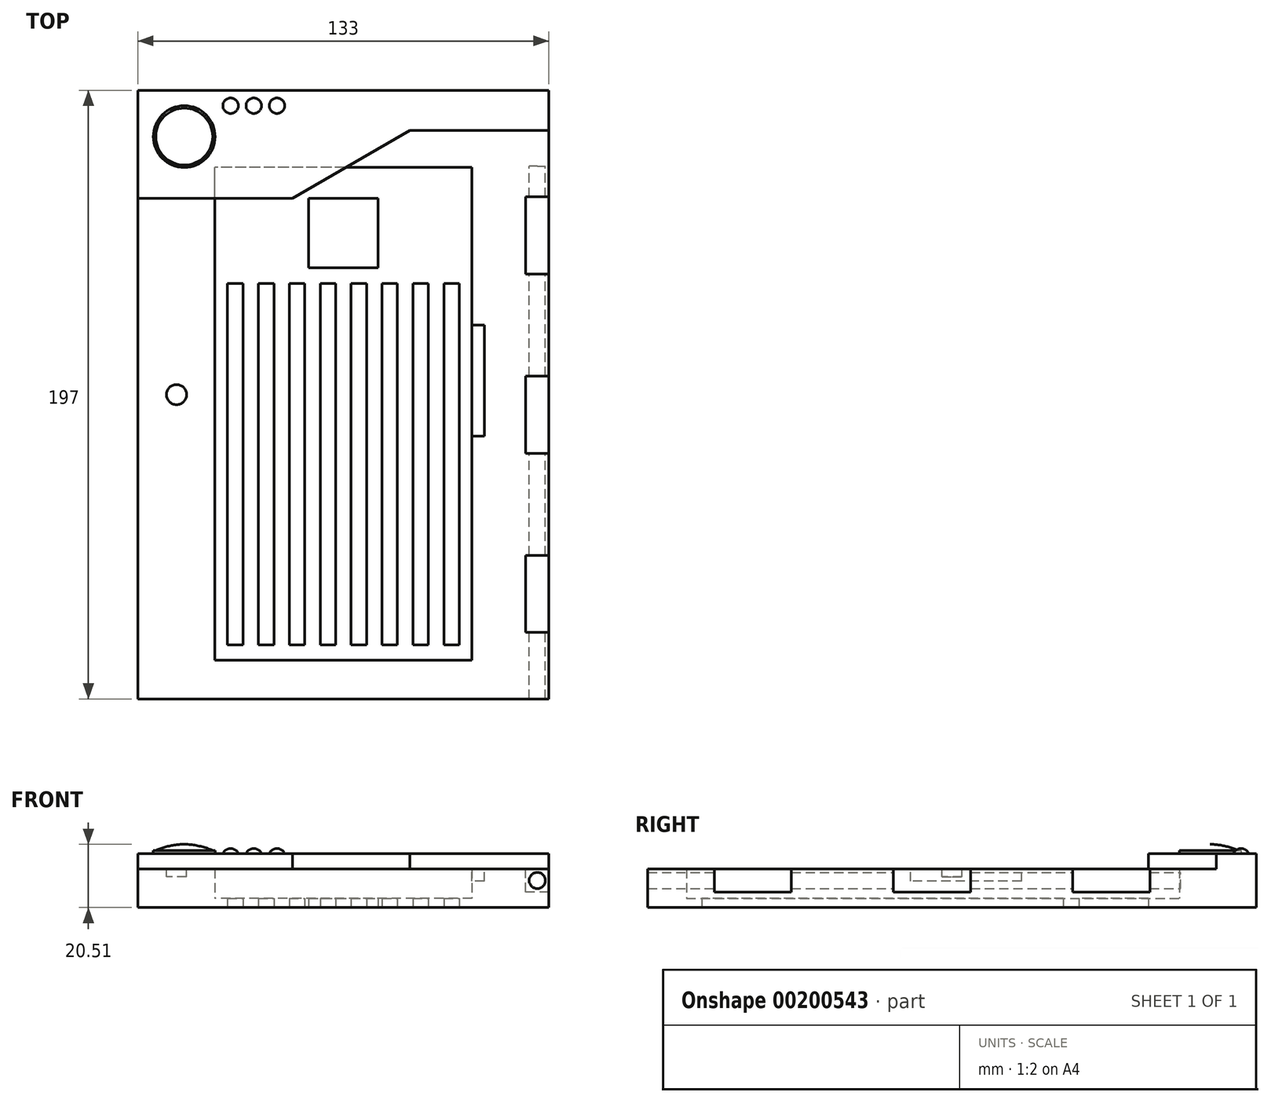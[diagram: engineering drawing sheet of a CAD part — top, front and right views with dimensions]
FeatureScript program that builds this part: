
annotation { "Feature Type Name" : "Feature", "Feature Type Description" : "" }
export const myFeature = defineFeature(function(context is Context, id is Id, definition is map)
    precondition{}
    {
        {
            var Q0;
            Q0=qCreatedBy(makeId("Top.planeOp"),FACE);
            var sketch = newSketch(context, id + "F0", { "sketchPlane" : qUnion([Q0])});
            skLineSegment(sketch, "E0.bottom", {"start": v(-77.75, 90.01) * mm, "end": v(55.25, 90.01) * mm});
            skLineSegment(sketch, "E0.top", {"start": v(-77.75, -106.99) * mm, "end": v(55.25, -106.99) * mm});
            skLineSegment(sketch, "E0.left", {"start": v(-77.75, 90.01) * mm, "end": v(-77.75, -106.99) * mm});
            skLineSegment(sketch, "E0.right", {"start": v(55.25, 90.01) * mm, "end": v(55.25, -106.99) * mm});
            skLineSegment(sketch, "E1.bottom", {"start": v(-52.88, 65.01) * mm, "end": v(30.38, 65.01) * mm});
            skLineSegment(sketch, "E1.top", {"start": v(-52.88, -94.49) * mm, "end": v(30.37, -94.49) * mm});
            skLineSegment(sketch, "E1.left", {"start": v(-52.88, 65.01) * mm, "end": v(-52.88, -94.49) * mm});
            skLineSegment(sketch, "E1.right", {"start": v(30.38, 65.01) * mm, "end": v(30.37, -94.49) * mm});
            skLineSegment(sketch, "E2", {"start": v(-77.75, 24.15) * mm, "end": v(-52.88, 24.15) * mm, "construction": true});
            skLineSegment(sketch, "E3", {"start": v(30.38, 23.5) * mm, "end": v(55.25, 23.5) * mm, "construction": true});
            skLineSegment(sketch, "E4.bottom", {"start": v(-22.5, 55.01) * mm, "end": v(0, 55.01) * mm});
            skLineSegment(sketch, "E4.top", {"start": v(-22.5, 32.51) * mm, "end": v(0, 32.51) * mm});
            skLineSegment(sketch, "E4.left", {"start": v(-22.5, 55.01) * mm, "end": v(-22.5, 32.51) * mm});
            skLineSegment(sketch, "E4.right", {"start": v(0, 55.01) * mm, "end": v(0, 32.51) * mm});
            skLineSegment(sketch, "E5", {"start": v(-22.5, 43.76) * mm, "end": v(-52.88, 43.76) * mm, "construction": true});
            skLineSegment(sketch, "E6", {"start": v(0, 43.76) * mm, "end": v(30.38, 43.76) * mm, "construction": true});
            skPoint(sketch, "E7.oppositeSnap0", {"position": v(30.37, -14.74) * mm});
            skLineSegment(sketch, "E8.bottom", {"start": v(-48.75, 27.51) * mm, "end": v(-43.75, 27.51) * mm});
            skLineSegment(sketch, "E8.top", {"start": v(-48.75, -89.49) * mm, "end": v(-43.75, -89.49) * mm});
            skLineSegment(sketch, "E8.left", {"start": v(-48.75, 27.51) * mm, "end": v(-48.75, -89.49) * mm});
            skLineSegment(sketch, "E8.right", {"start": v(-43.75, 27.51) * mm, "end": v(-43.75, -89.49) * mm});
            skLineSegment(sketch, "E9.1.0.0", {"start": v(-38.75, 27.51) * mm, "end": v(-38.75, -89.49) * mm});
            skLineSegment(sketch, "E9.1.0.1", {"start": v(-33.75, 27.51) * mm, "end": v(-33.75, -89.49) * mm});
            skLineSegment(sketch, "E9.1.0.2", {"start": v(-38.75, 27.51) * mm, "end": v(-33.75, 27.51) * mm});
            skLineSegment(sketch, "E9.1.0.3", {"start": v(-38.75, -89.49) * mm, "end": v(-33.75, -89.49) * mm});
            skLineSegment(sketch, "E9.2.0.0", {"start": v(-28.75, 27.51) * mm, "end": v(-28.75, -89.49) * mm});
            skLineSegment(sketch, "E9.2.0.1", {"start": v(-23.75, 27.51) * mm, "end": v(-23.75, -89.49) * mm});
            skLineSegment(sketch, "E9.2.0.2", {"start": v(-28.75, 27.51) * mm, "end": v(-23.75, 27.51) * mm});
            skLineSegment(sketch, "E9.2.0.3", {"start": v(-28.75, -89.49) * mm, "end": v(-23.75, -89.49) * mm});
            skLineSegment(sketch, "E9.3.0.0", {"start": v(-18.75, 27.51) * mm, "end": v(-18.75, -89.49) * mm});
            skLineSegment(sketch, "E9.3.0.1", {"start": v(-13.75, 27.51) * mm, "end": v(-13.75, -89.49) * mm});
            skLineSegment(sketch, "E9.3.0.2", {"start": v(-18.75, 27.51) * mm, "end": v(-13.75, 27.51) * mm});
            skLineSegment(sketch, "E9.3.0.3", {"start": v(-18.75, -89.49) * mm, "end": v(-13.75, -89.49) * mm});
            skLineSegment(sketch, "E9.4.0.0", {"start": v(-8.75, 27.51) * mm, "end": v(-8.75, -89.49) * mm});
            skLineSegment(sketch, "E9.4.0.1", {"start": v(-3.75, 27.51) * mm, "end": v(-3.75, -89.49) * mm});
            skLineSegment(sketch, "E9.4.0.2", {"start": v(-8.75, 27.51) * mm, "end": v(-3.75, 27.51) * mm});
            skLineSegment(sketch, "E9.4.0.3", {"start": v(-8.75, -89.49) * mm, "end": v(-3.75, -89.49) * mm});
            skLineSegment(sketch, "E9.5.0.0", {"start": v(1.25, 27.51) * mm, "end": v(1.25, -89.49) * mm});
            skLineSegment(sketch, "E9.5.0.1", {"start": v(6.25, 27.51) * mm, "end": v(6.25, -89.49) * mm});
            skLineSegment(sketch, "E9.5.0.2", {"start": v(1.25, 27.51) * mm, "end": v(6.25, 27.51) * mm});
            skLineSegment(sketch, "E9.5.0.3", {"start": v(1.25, -89.49) * mm, "end": v(6.25, -89.49) * mm});
            skLineSegment(sketch, "E9.6.0.0", {"start": v(11.25, 27.51) * mm, "end": v(11.25, -89.49) * mm});
            skLineSegment(sketch, "E9.6.0.1", {"start": v(16.25, 27.51) * mm, "end": v(16.25, -89.49) * mm});
            skLineSegment(sketch, "E9.6.0.2", {"start": v(11.25, 27.51) * mm, "end": v(16.25, 27.51) * mm});
            skLineSegment(sketch, "E9.6.0.3", {"start": v(11.25, -89.49) * mm, "end": v(16.25, -89.49) * mm});
            skLineSegment(sketch, "E9.7.0.0", {"start": v(21.25, 27.51) * mm, "end": v(21.25, -89.49) * mm});
            skLineSegment(sketch, "E9.7.0.1", {"start": v(26.25, 27.51) * mm, "end": v(26.25, -89.49) * mm});
            skLineSegment(sketch, "E9.7.0.2", {"start": v(21.25, 27.51) * mm, "end": v(26.25, 27.51) * mm});
            skLineSegment(sketch, "E9.7.0.3", {"start": v(21.25, -89.49) * mm, "end": v(26.25, -89.49) * mm});
            skLineSegment(sketch, "E9.direction1", {"start": v(-48.75, -89.49) * mm, "end": v(-38.75, -89.49) * mm, "construction": true});
            skSolve(sketch);
        }
        {
            var Q0;
            Q0=makeQuery(id+"F0.imprint","IMPRINT",FACE,{"disambiguationData":[TD([[makeQuery(id+"F0.imprint","IMPRINT",EDGE,{"derivedFrom":sQuery(id+"F0.wireOp",EDGE,"E0.bottom")}),-1.0]])]});
            var Q1;
            Q1=makeQuery(id+"F0.imprint","IMPRINT",FACE,{"disambiguationData":[TD([[makeQuery(id+"F0.imprint","IMPRINT",EDGE,{"derivedFrom":sQuery(id+"F0.wireOp",EDGE,"E1.bottom")}),-1.0]])]});
            extrude(context, id + "F1", {"entities" : qUnion([Q0, Q1]), "depth" : 3 * mm});
        }
        {
            var Q0;
            Q0 = qSketchRegion(id + "F0", true);
            extrude(context, id + "F2", {"entities" : qUnion([Q0]), "operationType" : NewBodyOperationType.ADD, "depth" : 12.5 * mm});
        }
        {
            var Q0;
            Q0=makeQuery(id+"F2.opExtrude","CAP_FACE",FACE,{"disambiguationData":[OSD([sQuery(id+"F0.wireOp",EDGE,"E0.bottom"),sQuery(id+"F0.wireOp",EDGE,"E0.top"),sQuery(id+"F0.wireOp",EDGE,"E0.left"),sQuery(id+"F0.wireOp",EDGE,"E0.right"),sQuery(id+"F0.wireOp",EDGE,"E1.bottom"),sQuery(id+"F0.wireOp",EDGE,"E1.top"),sQuery(id+"F0.wireOp",EDGE,"E1.left"),sQuery(id+"F0.wireOp",EDGE,"E1.right")])],"isStart":false});
            var sketch = newSketch(context, id + "F3", { "sketchPlane" : qUnion([Q0])});
            skLineSegment(sketch, "E10", {"start": v(-65.25, 90.01) * mm, "end": v(-65.25, -11.74) * mm, "construction": true});
            skCircle(sketch, "E11", {"center": v(-65.25, -8.49) * mm, "radius": 3.25 * mm});
            skLineSegment(sketch, "E12.trimOffspring", {"start": v(-65.25, -5.24) * mm, "end": v(-65.25, -106.99) * mm, "construction": true});
            skLineSegment(sketch, "E13", {"start": v(-77.75, 55.01) * mm, "end": v(-27.75, 55.01) * mm});
            skLineSegment(sketch, "E14", {"start": v(-27.75, 55.01) * mm, "end": v(10.25, 77.01) * mm});
            skLineSegment(sketch, "E15", {"start": v(10.25, 77.01) * mm, "end": v(55.25, 77.01) * mm});
            skLineSegment(sketch, "E16", {"start": v(-77.75, 55.01) * mm, "end": v(-77.75, 90.01) * mm});
            skLineSegment(sketch, "E17", {"start": v(-77.75, 90.01) * mm, "end": v(55.25, 90.01) * mm});
            skLineSegment(sketch, "E18", {"start": v(55.25, 90.01) * mm, "end": v(55.25, 77.01) * mm});
            skSolve(sketch);
        }
        {
            var Q0;
            Q0=makeQuery(id+"F3.imprint","IMPRINT",FACE,{"disambiguationData":[TD([[makeQuery(id+"F3.imprint","IMPRINT",EDGE,{"derivedFrom":sQuery(id+"F3.wireOp",EDGE,"E11")}),1.0]])]});
            var Q1;
            {var subQ4=sQuery(id+"F3.wireOp",EDGE,"E15");Q1=makeQuery(id+"F3.imprint","IMPRINT",FACE,{"disambiguationData":[TD([[makeQuery(id+"F3.imprint","IMPRINT",EDGE,{"derivedFrom":subQ4}),1.0]])]});}
            extrude(context, id + "F4", {"entities" : qUnion([Q0, Q1]), "operationType" : NewBodyOperationType.REMOVE, "oppositeDirection" : true, "depth" : 2.5 * mm});
        }
        {
            var Q0;
            {var subQ4=sQuery(id+"F3.wireOp",EDGE,"E15");Q0=makeQuery(id+"F3.imprint","IMPRINT",FACE,{"disambiguationData":[TD([[makeQuery(id+"F3.imprint","IMPRINT",EDGE,{"derivedFrom":subQ4}),1.0]])]});}
            var Q1;
            {var subQ0=sQuery(id+"F3.wireOp",EDGE,"E14");var subQ1=sQuery(id+"F3.wireOp",EDGE,"E13");var subQ2=makeQuery(id+"F3.imprint","INTERSECT",VERTEX,{"derivedFrom":[subQ1,subQ0]});Q1=makeQuery(id+"F3.imprint","IMPRINT",FACE,{"disambiguationData":[TD([[makeQuery(id+"F3.imprint","IMPRINT",EDGE,{"disambiguationData":[TD([[subQ2,1.0]])],"derivedFrom":subQ1}),1.0]])]});}
            var Q2;
            Q2=makeQuery(id+"F4.boolean.opBoolean","COPY",FACE,{"derivedFrom":makeQuery(id+"F4.opExtrude","CAP_FACE",FACE,{"disambiguationData":[OSD([sQuery(id+"F3.wireOp",EDGE,"E13"),sQuery(id+"F3.wireOp",EDGE,"E14"),sQuery(id+"F3.wireOp",EDGE,"E15"),sQuery(id+"F3.wireOp",EDGE,"E16"),sQuery(id+"F3.wireOp",EDGE,"E17"),sQuery(id+"F3.wireOp",EDGE,"E18")])],"isStart":false})});
            extrude(context, id + "F5", {"entities" : qUnion([Q0, Q1, Q2]), "operationType" : NewBodyOperationType.ADD, "depth" : 5 * mm});
        }
        {
            var Q0;
            {var subQ0=sQuery(id+"F3.wireOp",EDGE,"E18");var subQ1=sQuery(id+"F3.wireOp",EDGE,"E17");var subQ2=sQuery(id+"F3.wireOp",EDGE,"E16");var subQ3=sQuery(id+"F3.wireOp",EDGE,"E15");var subQ4=sQuery(id+"F3.wireOp",EDGE,"E14");var subQ6=sQuery(id+"F3.wireOp",EDGE,"E13");var subQ7=makeQuery(id+"F3.imprint","INTERSECT",VERTEX,{"derivedFrom":[subQ6,subQ4]});var subQ8=makeQuery(id+"F3.imprint","INTERSECT",VERTEX,{"derivedFrom":[makeQuery(id+"F2.opExtrude","CAP_EDGE",EDGE,{"disambiguationData":[OSD([sQuery(id+"F0.wireOp",EDGE,"E1.left")])],"isStart":false}),subQ6]});Q0=makeQuery(id+"F5.opExtrude","CAP_FACE",FACE,{"disambiguationData":[OSD([subQ6,subQ4,subQ3,subQ2,subQ1,subQ0]),TDD([makeQuery(id+"F3.imprint","IMPRINT",EDGE,{"disambiguationData":[TD([[subQ8,1.0]])],"derivedFrom":subQ6}),makeQuery(id+"F3.imprint","IMPRINT",EDGE,{"disambiguationData":[TD([[subQ7,1.0]])],"derivedFrom":subQ6}),makeQuery(id+"F3.imprint","IMPRINT",EDGE,{"disambiguationData":[TD([[subQ7,-1.0]])],"derivedFrom":subQ4}),makeQuery(id+"F3.imprint","IMPRINT",EDGE,{"disambiguationData":[TD([[makeQuery(id+"F3.imprint","INTERSECT",VERTEX,{"derivedFrom":[subQ4,subQ3]}),1.0]])],"derivedFrom":subQ4}),makeQuery(id+"F3.imprint","IMPRINT",EDGE,{"derivedFrom":subQ3}),makeQuery(id+"F3.imprint","IMPRINT",EDGE,{"derivedFrom":subQ2}),makeQuery(id+"F3.imprint","IMPRINT",EDGE,{"derivedFrom":subQ1}),makeQuery(id+"F3.imprint","IMPRINT",EDGE,{"derivedFrom":subQ0})])],"isStart":false});}
            var sketch = newSketch(context, id + "F6", { "sketchPlane" : qUnion([Q0])});
            skCircle(sketch, "E19", {"center": v(-62.75, 75.01) * mm, "radius": 10 * mm});
            skCircle(sketch, "E20", {"center": v(-47.75, 85.01) * mm, "radius": 2.5 * mm});
            skCircle(sketch, "E21", {"center": v(-40.25, 85.01) * mm, "radius": 2.5 * mm});
            skCircle(sketch, "E22", {"center": v(-32.75, 85.01) * mm, "radius": 2.5 * mm});
            skLineSegment(sketch, "E23", {"start": v(-47.75, 85.01) * mm, "end": v(-32.75, 85.01) * mm, "construction": true});
            skLineSegment(sketch, "E24", {"start": v(-77.75, 90.01) * mm, "end": v(55.25, 90.01) * mm, "construction": true});
            skLineSegment(sketch, "E25", {"start": v(-77.75, 90.01) * mm, "end": v(-77.75, 55.01) * mm});
            skSolve(sketch);
        }
        {
            var Q0;
            Q0=makeQuery(id+"F6.imprint","IMPRINT",FACE,{"disambiguationData":[TD([[makeQuery(id+"F6.imprint","IMPRINT",EDGE,{"derivedFrom":sQuery(id+"F6.wireOp",EDGE,"E19")}),1.0]])]});
            extrude(context, id + "F7", {"entities" : qUnion([Q0]), "operationType" : NewBodyOperationType.ADD, "depth" : 1 * mm});
        }
        {
            var Q0;
            {var subQ0=sQuery(id+"F3.wireOp",EDGE,"E13");var subQ1=makeQuery(id+"F3.imprint","INTERSECT",VERTEX,{"derivedFrom":[makeQuery(id+"F2.opExtrude","CAP_EDGE",EDGE,{"disambiguationData":[OSD([sQuery(id+"F0.wireOp",EDGE,"E1.left")])],"isStart":false}),subQ0]});Q0=makeQuery(id+"F5.boolean.opBoolean","MERGE",FACE,{"derivedFrom":[makeQuery(id+"F5.opExtrude","SWEPT_FACE",FACE,{"disambiguationData":[OSD([subQ0]),TDD([makeQuery(id+"F3.imprint","IMPRINT",EDGE,{"disambiguationData":[TD([[subQ1,1.0]])],"derivedFrom":subQ0}),makeQuery(id+"F3.imprint","IMPRINT",EDGE,{"disambiguationData":[TD([[makeQuery(id+"F3.imprint","INTERSECT",VERTEX,{"derivedFrom":[subQ0,sQuery(id+"F3.wireOp",EDGE,"E14")]}),1.0]])],"derivedFrom":subQ0})])]}),makeQuery(id+"F5.opExtrude","SWEPT_FACE",FACE,{"disambiguationData":[OSD([subQ0]),TDD([makeQuery(id+"F4.boolean.opBoolean","COPY",EDGE,{"derivedFrom":makeQuery(id+"F4.opExtrude","CAP_EDGE",EDGE,{"disambiguationData":[OSD([subQ0])],"isStart":false})})])]})]});}
            cPlane(context, id + "F8", {"entities" : qUnion([Q0]), "cplaneType" : CPlaneType.OFFSET, "offset" : 20 * mm, "oppositeDirection" : true, "width" : 150 * mm, "height" : 150 * mm});
        }
        {
            var Q0;
            Q0=qCreatedBy(id+"F8.planeOp",FACE);
            var sketch = newSketch(context, id + "F9", { "sketchPlane" : qUnion([Q0])});
            skLineSegment(sketch, "E26", {"start": v(-72.75, 18.5) * mm, "end": v(-62.75, 18.5) * mm});
            skPoint(sketch, "E27", {"position": v(-62.75, 18.5) * mm});
            skArc(sketch, "E28", {"start": v(-62.75, 20.5) * mm, "mid": v(-67.45, 19.94) * mm, "end": v(-71.95, 18.5) * mm});
            skLineSegment(sketch, "E29", {"start": v(-62.75, 18.5) * mm, "end": v(-62.75, 20.5) * mm});
            skPoint(sketch, "E30.trimOffspring.end.orphan", {"position": v(-52.75, 18.5) * mm});
            skSolve(sketch);
        }
        {
            var Q0;
            {var subQ2=sQuery(id+"F9.wireOp",EDGE,"E28");Q0=makeQuery(id+"F9.imprint","IMPRINT",FACE,{"disambiguationData":[TD([[makeQuery(id+"F9.imprint","IMPRINT",EDGE,{"derivedFrom":subQ2}),1.0]])]});}
            var Q1;
            Q1=sQuery(id+"F9.wireOp",EDGE,"E29");
            revolve(context, id + "F10", {"operationType" : NewBodyOperationType.ADD, "entities" : qUnion([Q0]), "axis" : qUnion([Q1]), "revolveType" : RevolveType.FULL});
        }
        {
            var Q0;
            {var subQ0=sQuery(id+"F3.wireOp",EDGE,"E13");var subQ1=makeQuery(id+"F3.imprint","INTERSECT",VERTEX,{"derivedFrom":[makeQuery(id+"F2.opExtrude","CAP_EDGE",EDGE,{"disambiguationData":[OSD([sQuery(id+"F0.wireOp",EDGE,"E1.left")])],"isStart":false}),subQ0]});Q0=makeQuery(id+"F5.boolean.opBoolean","MERGE",FACE,{"derivedFrom":[makeQuery(id+"F5.opExtrude","SWEPT_FACE",FACE,{"disambiguationData":[OSD([subQ0]),TDD([makeQuery(id+"F3.imprint","IMPRINT",EDGE,{"disambiguationData":[TD([[subQ1,1.0]])],"derivedFrom":subQ0}),makeQuery(id+"F3.imprint","IMPRINT",EDGE,{"disambiguationData":[TD([[makeQuery(id+"F3.imprint","INTERSECT",VERTEX,{"derivedFrom":[subQ0,sQuery(id+"F3.wireOp",EDGE,"E14")]}),1.0]])],"derivedFrom":subQ0})])]}),makeQuery(id+"F5.opExtrude","SWEPT_FACE",FACE,{"disambiguationData":[OSD([subQ0]),TDD([makeQuery(id+"F4.boolean.opBoolean","COPY",EDGE,{"derivedFrom":makeQuery(id+"F4.opExtrude","CAP_EDGE",EDGE,{"disambiguationData":[OSD([subQ0])],"isStart":false})})])]})]});}
            cPlane(context, id + "F11", {"entities" : qUnion([Q0]), "cplaneType" : CPlaneType.OFFSET, "offset" : 30 * mm, "oppositeDirection" : true, "width" : 150 * mm, "height" : 150 * mm});
        }
        {
            var Q0;
            Q0=qCreatedBy(id+"F11.planeOp",FACE);
            var sketch = newSketch(context, id + "F12", { "sketchPlane" : qUnion([Q0])});
            skLineSegment(sketch, "E31", {"start": v(-50.25, 17.5) * mm, "end": v(-47.75, 17.5) * mm});
            skLineSegment(sketch, "E32", {"start": v(-45.25, 19.64) * mm, "end": v(-45.25, 16.03) * mm, "construction": true});
            skLineSegment(sketch, "E33", {"start": v(-42.75, 20.33) * mm, "end": v(-42.75, 15.6) * mm, "construction": true});
            skLineSegment(sketch, "E34", {"start": v(-37.75, 20.73) * mm, "end": v(-37.75, 15.6) * mm, "construction": true});
            skLineSegment(sketch, "E35", {"start": v(-35.25, 20.57) * mm, "end": v(-35.25, 15.22) * mm, "construction": true});
            skLineSegment(sketch, "E36.trimOffspring", {"start": v(-35.25, 17.5) * mm, "end": v(-32.75, 17.5) * mm});
            skLineSegment(sketch, "E37.trimOffspring", {"start": v(-42.75, 17.5) * mm, "end": v(-40.25, 17.5) * mm});
            skPoint(sketch, "E38", {"position": v(-47.75, 17.5) * mm});
            skPoint(sketch, "E39", {"position": v(-40.25, 17.5) * mm});
            skArc(sketch, "E40", {"start": v(-47.75, 19.1) * mm, "mid": v(-49.24, 18.67) * mm, "end": v(-50.25, 17.5) * mm});
            skLineSegment(sketch, "E41", {"start": v(-37.75, 17.5) * mm, "end": v(-37.75, 17.5) * mm});
            skLineSegment(sketch, "E42", {"start": v(-30.25, 21.7) * mm, "end": v(-30.25, 16.35) * mm, "construction": true});
            skPoint(sketch, "E43", {"position": v(-32.75, 17.5) * mm});
            skArc(sketch, "E44", {"start": v(-32.75, 19.1) * mm, "mid": v(-34.24, 18.67) * mm, "end": v(-35.25, 17.5) * mm});
            skLineSegment(sketch, "E45", {"start": v(-32.75, 17.5) * mm, "end": v(-32.75, 19.1) * mm});
            skLineSegment(sketch, "E46", {"start": v(-40.25, 17.5) * mm, "end": v(-40.25, 19.1) * mm});
            skLineSegment(sketch, "E47", {"start": v(-47.75, 17.5) * mm, "end": v(-47.75, 19.1) * mm});
            skPoint(sketch, "E48.orphan", {"position": v(-45.25, 17.5) * mm});
            skArc(sketch, "E49.trimOffspring", {"start": v(-40.25, 19.1) * mm, "mid": v(-41.74, 18.67) * mm, "end": v(-42.75, 17.5) * mm});
            skPoint(sketch, "E50.orphan", {"position": v(-30.25, 17.5) * mm});
            skSolve(sketch);
        }
        {
            var Q0;
            Q0=makeQuery(id+"F12.imprint","IMPRINT",FACE,{"disambiguationData":[TD([[makeQuery(id+"F12.imprint","IMPRINT",EDGE,{"derivedFrom":sQuery(id+"F12.wireOp",EDGE,"E31")}),1.0]])]});
            var Q1;
            Q1=sQuery(id+"F12.wireOp",EDGE,"E47");
            revolve(context, id + "F13", {"operationType" : NewBodyOperationType.ADD, "entities" : qUnion([Q0]), "axis" : qUnion([Q1]), "revolveType" : RevolveType.FULL});
        }
        {
            var Q0;
            Q0=makeQuery(id+"F12.imprint","IMPRINT",FACE,{"disambiguationData":[TD([[makeQuery(id+"F12.imprint","IMPRINT",EDGE,{"derivedFrom":sQuery(id+"F12.wireOp",EDGE,"E37.trimOffspring")}),1.0]])]});
            var Q1;
            Q1=sQuery(id+"F12.wireOp",EDGE,"E46");
            revolve(context, id + "F14", {"operationType" : NewBodyOperationType.ADD, "entities" : qUnion([Q0]), "axis" : qUnion([Q1]), "revolveType" : RevolveType.FULL});
        }
        {
            var Q0;
            Q0=makeQuery(id+"F12.imprint","IMPRINT",FACE,{"disambiguationData":[TD([[makeQuery(id+"F12.imprint","IMPRINT",EDGE,{"derivedFrom":sQuery(id+"F12.wireOp",EDGE,"E36.trimOffspring")}),1.0]])]});
            var Q1;
            Q1=sQuery(id+"F12.wireOp",EDGE,"E45");
            revolve(context, id + "F15", {"operationType" : NewBodyOperationType.ADD, "entities" : qUnion([Q0]), "axis" : qUnion([Q1]), "revolveType" : RevolveType.FULL});
        }
        {
            var Q0;
            Q0=makeQuery(id+"F2.opExtrude","CAP_FACE",FACE,{"disambiguationData":[OSD([sQuery(id+"F0.wireOp",EDGE,"E0.bottom"),sQuery(id+"F0.wireOp",EDGE,"E0.top"),sQuery(id+"F0.wireOp",EDGE,"E0.left"),sQuery(id+"F0.wireOp",EDGE,"E0.right"),sQuery(id+"F0.wireOp",EDGE,"E1.bottom"),sQuery(id+"F0.wireOp",EDGE,"E1.top"),sQuery(id+"F0.wireOp",EDGE,"E1.left"),sQuery(id+"F0.wireOp",EDGE,"E1.right")])],"isStart":false});
            var sketch = newSketch(context, id + "F16", { "sketchPlane" : qUnion([Q0])});
            skLineSegment(sketch, "E51.bottom", {"start": v(55.25, 55.51) * mm, "end": v(47.75, 55.51) * mm});
            skLineSegment(sketch, "E51.top", {"start": v(55.25, 30.51) * mm, "end": v(47.75, 30.51) * mm});
            skLineSegment(sketch, "E51.left", {"start": v(55.25, 55.51) * mm, "end": v(55.25, 30.51) * mm});
            skLineSegment(sketch, "E51.right", {"start": v(47.75, 55.51) * mm, "end": v(47.75, 30.51) * mm});
            skLineSegment(sketch, "E52.0.1.0", {"start": v(55.25, -2.49) * mm, "end": v(47.75, -2.49) * mm});
            skLineSegment(sketch, "E52.0.1.1", {"start": v(55.25, -27.49) * mm, "end": v(47.75, -27.49) * mm});
            skLineSegment(sketch, "E52.0.1.2", {"start": v(47.75, -2.49) * mm, "end": v(47.75, -27.49) * mm});
            skLineSegment(sketch, "E52.0.1.3", {"start": v(55.25, -2.49) * mm, "end": v(55.25, -27.49) * mm});
            skLineSegment(sketch, "E52.0.2.0", {"start": v(55.25, -60.49) * mm, "end": v(47.75, -60.49) * mm});
            skLineSegment(sketch, "E52.0.2.1", {"start": v(55.25, -85.49) * mm, "end": v(47.75, -85.49) * mm});
            skLineSegment(sketch, "E52.0.2.2", {"start": v(47.75, -60.49) * mm, "end": v(47.75, -85.49) * mm});
            skLineSegment(sketch, "E52.0.2.3", {"start": v(55.25, -60.49) * mm, "end": v(55.25, -85.49) * mm});
            skLineSegment(sketch, "E52.direction1", {"start": v(47.75, 30.51) * mm, "end": v(75.25, 30.51) * mm, "construction": true});
            skLineSegment(sketch, "E52.direction2", {"start": v(47.75, 30.51) * mm, "end": v(47.75, -27.49) * mm, "construction": true});
            skLineSegment(sketch, "E53", {"start": v(-77.75, -106.99) * mm, "end": v(-77.75, 55.01) * mm});
            skLineSegment(sketch, "E54", {"start": v(-77.75, -106.99) * mm, "end": v(55.25, -106.99) * mm});
            skLineSegment(sketch, "E55", {"start": v(55.25, 77.01) * mm, "end": v(55.25, -106.99) * mm, "construction": true});
            skLineSegment(sketch, "E56.bottom", {"start": v(34.37, 14.01) * mm, "end": v(30.37, 14.01) * mm});
            skLineSegment(sketch, "E56.top", {"start": v(34.37, -21.99) * mm, "end": v(30.37, -21.99) * mm});
            skLineSegment(sketch, "E56.left", {"start": v(34.37, 14.01) * mm, "end": v(34.38, -21.99) * mm});
            skLineSegment(sketch, "E56.right", {"start": v(30.37, 14.01) * mm, "end": v(30.37, -21.99) * mm});
            skSolve(sketch);
        }
        {
            var Q0;
            Q0=makeQuery(id+"F16.imprint","IMPRINT",FACE,{"disambiguationData":[TD([[makeQuery(id+"F16.imprint","IMPRINT",EDGE,{"derivedFrom":sQuery(id+"F16.wireOp",EDGE,"E51.bottom")}),1.0]])]});
            var Q1;
            Q1=makeQuery(id+"F16.imprint","IMPRINT",FACE,{"disambiguationData":[TD([[makeQuery(id+"F16.imprint","IMPRINT",EDGE,{"derivedFrom":sQuery(id+"F16.wireOp",EDGE,"E52.0.1.0")}),1.0]])]});
            var Q2;
            Q2=makeQuery(id+"F16.imprint","IMPRINT",FACE,{"disambiguationData":[TD([[makeQuery(id+"F16.imprint","IMPRINT",EDGE,{"derivedFrom":sQuery(id+"F16.wireOp",EDGE,"E52.0.2.0")}),1.0]])]});
            extrude(context, id + "F17", {"entities" : qUnion([Q0, Q1, Q2]), "operationType" : NewBodyOperationType.REMOVE, "oppositeDirection" : true, "depth" : 7.5 * mm});
        }
        {
            var Q0;
            Q0=makeQuery(id+"F17.boolean.opBoolean","COPY",FACE,{"derivedFrom":makeQuery(id+"F17.opExtrude","SWEPT_FACE",FACE,{"disambiguationData":[OSD([sQuery(id+"F16.wireOp",EDGE,"E51.bottom")])]})});
            var sketch = newSketch(context, id + "F18", { "sketchPlane" : qUnion([Q0])});
            skPoint(sketch, "E57", {"position": v(51.5, 8.75) * mm});
            skCircle(sketch, "E58", {"center": v(51.5, 8.75) * mm, "radius": 2.62 * mm});
            skSolve(sketch);
        }
        {
            var Q0;
            Q0=makeQuery(id+"F18.imprint","IMPRINT",FACE,{"disambiguationData":[TD([[makeQuery(id+"F18.imprint","IMPRINT",EDGE,{"derivedFrom":sQuery(id+"F18.wireOp",EDGE,"E58")}),1.0]])]});
            extrude(context, id + "F19", {"entities" : qUnion([Q0]), "operationType" : NewBodyOperationType.REMOVE, "endBound" : BoundingType.THROUGH_ALL, "depth" : 1000 * mm, "hasSecondDirection" : true, "secondDirectionOppositeDirection" : true, "secondDirectionDepth" : 10 * mm});
        }
        {
            var Q0;
            Q0=makeQuery(id+"F16.imprint","IMPRINT",FACE,{"disambiguationData":[TD([[makeQuery(id+"F16.imprint","IMPRINT",EDGE,{"derivedFrom":sQuery(id+"F16.wireOp",EDGE,"E56.bottom")}),1.0]])]});
            extrude(context, id + "F20", {"entities" : qUnion([Q0]), "operationType" : NewBodyOperationType.REMOVE, "oppositeDirection" : true, "depth" : 4 * mm});
        }
    });
